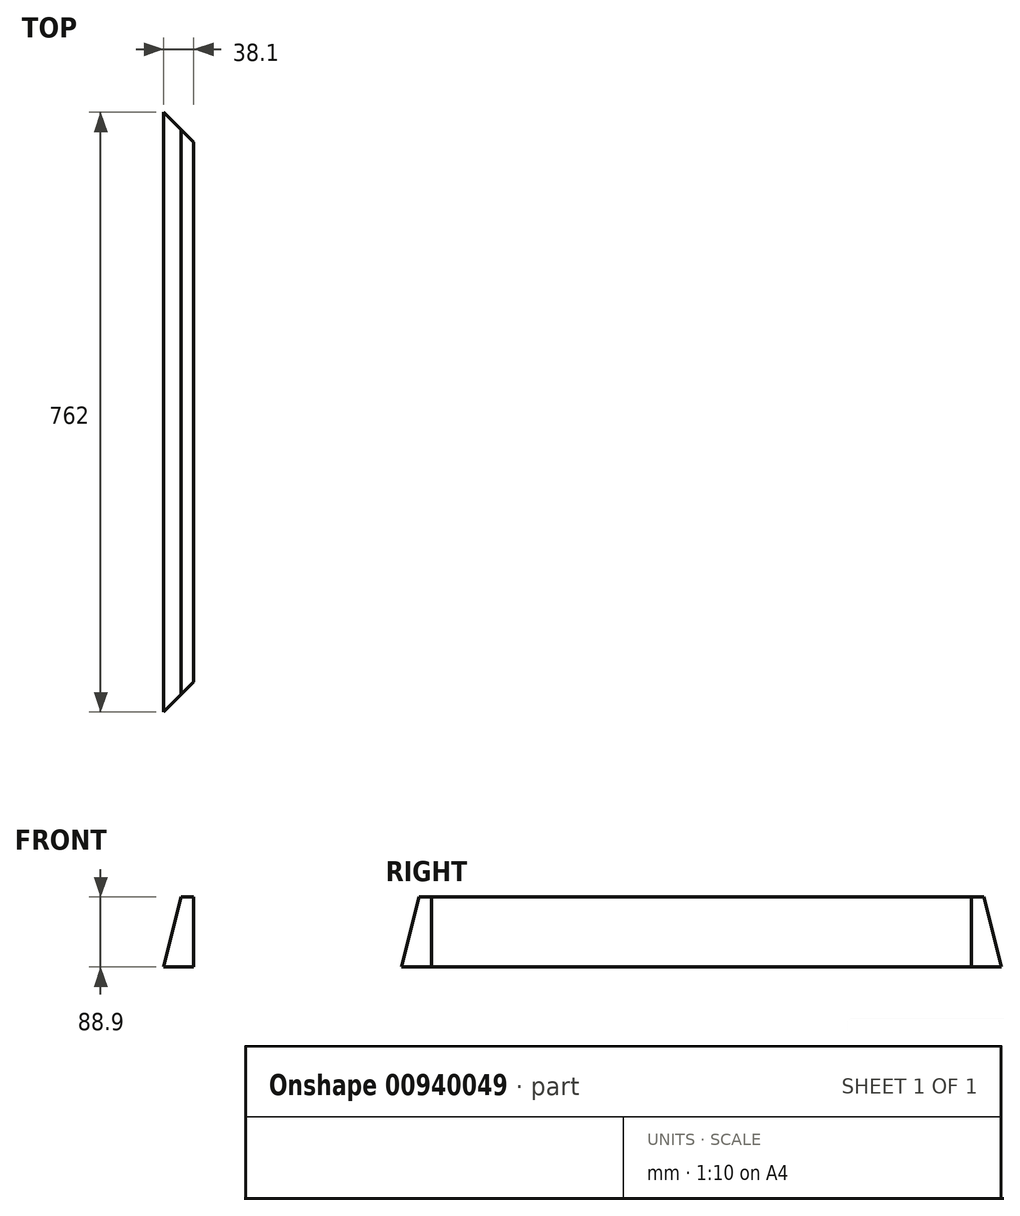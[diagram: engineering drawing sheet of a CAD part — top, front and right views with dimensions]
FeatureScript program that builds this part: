
annotation { "Feature Type Name" : "Feature", "Feature Type Description" : "" }
export const myFeature = defineFeature(function(context is Context, id is Id, definition is map)
    precondition{}
    {
        {
            var Q0;
            Q0=qCreatedBy(makeId("Front.planeOp"),FACE);
            var sketch = newSketch(context, id + "F0", { "sketchPlane" : qUnion([Q0])});
            skLineSegment(sketch, "E0.bottom", {"start": v(38.1, 44.45) * mm, "end": v(-38.1, 44.45) * mm});
            skLineSegment(sketch, "E0.top", {"start": v(38.1, -44.45) * mm, "end": v(-38.1, -44.45) * mm});
            skLineSegment(sketch, "E0.left", {"start": v(44.45, 38.1) * mm, "end": v(44.45, -38.1) * mm});
            skLineSegment(sketch, "E0.right", {"start": v(-44.45, 38.1) * mm, "end": v(-44.45, -38.1) * mm});
            skPoint(sketch, "E0.middle", {"position": v(0, 0) * mm});
            skPoint(sketch, "E1.visualSharp", {"position": v(-44.45, 44.45) * mm});
            skArc(sketch, "E1.filletArc", {"start": v(-38.1, 44.45) * mm, "mid": v(-42.6, 42.6) * mm, "end": v(-44.45, 38.1) * mm});
            skPoint(sketch, "E2.visualSharp", {"position": v(44.45, 44.45) * mm});
            skArc(sketch, "E2.filletArc", {"start": v(44.45, 38.1) * mm, "mid": v(42.6, 42.6) * mm, "end": v(38.1, 44.45) * mm});
            skPoint(sketch, "E3.visualSharp", {"position": v(44.45, -44.45) * mm});
            skArc(sketch, "E3.filletArc", {"start": v(38.1, -44.45) * mm, "mid": v(42.6, -42.6) * mm, "end": v(44.45, -38.1) * mm});
            skPoint(sketch, "E4.visualSharp", {"position": v(-44.45, -44.45) * mm});
            skArc(sketch, "E4.filletArc", {"start": v(-44.45, -38.1) * mm, "mid": v(-42.6, -42.6) * mm, "end": v(-38.1, -44.45) * mm});
            skLineSegment(sketch, "E5", {"start": v(0, -44.45) * mm, "end": v(0, 107.95) * mm});
            skLineSegment(sketch, "E6", {"start": v(0, 107.95) * mm, "end": v(38.1, -44.45) * mm});
            skLineSegment(sketch, "E7", {"start": v(0, 107.95) * mm, "end": v(-38.1, -44.45) * mm});
            skSolve(sketch);
        }
        {
            var Q0;
            {var subQ3=sQuery(id+"F0.wireOp",EDGE,"E0.bottom");var subQ7=sQuery(id+"F0.wireOp",EDGE,"E7");var subQ9=makeQuery(id+"F0.imprint","INTERSECT",VERTEX,{"derivedFrom":[subQ3,subQ7]});Q0=makeQuery(id+"F0.imprint","IMPRINT",FACE,{"disambiguationData":[TD([[makeQuery(id+"F0.imprint","IMPRINT",EDGE,{"disambiguationData":[TD([[subQ9,1.0]])],"derivedFrom":subQ3}),1.0]])]});}
            extrude(context, id + "F1", {"entities" : qUnion([Q0]), "depth" : 762 * mm, "offsetDistance" : 25.4 * mm});
        }
        {
            var Q0;
            Q0=makeQuery(id+"F1.opExtrude","SWEPT_FACE",FACE,{"disambiguationData":[OSD([sQuery(id+"F0.wireOp",EDGE,"E0.top")])]});
            var sketch = newSketch(context, id + "F2", { "sketchPlane" : qUnion([Q0])});
            skLineSegment(sketch, "E8", {"start": v(-38.1, 0) * mm, "end": v(0, 38.1) * mm});
            skLineSegment(sketch, "E9.0", {"start": v(0, 762) * mm, "end": v(0, 0) * mm});
            skLineSegment(sketch, "E10.0", {"start": v(0, 0) * mm, "end": v(-38.1, 0) * mm});
            skLineSegment(sketch, "E11", {"start": v(-38.1, 381) * mm, "end": v(0, 381) * mm});
            skLineSegment(sketch, "E12.MirrorCS", {"start": v(-38.1, 762) * mm, "end": v(0, 723.9) * mm});
            skSolve(sketch);
        }
        {
            var Q0;
            {var subQ2=sQuery(id+"F2.wireOp",EDGE,"E12.MirrorCS");Q0=makeQuery(id+"F2.imprint","IMPRINT",FACE,{"disambiguationData":[TD([[makeQuery(id+"F2.imprint","IMPRINT",EDGE,{"derivedFrom":subQ2}),1.0]])]});}
            var Q1;
            {var subQ0=sQuery(id+"F2.wireOp",EDGE,"E8");Q1=makeQuery(id+"F2.imprint","IMPRINT",FACE,{"disambiguationData":[TD([[makeQuery(id+"F2.imprint","IMPRINT",EDGE,{"derivedFrom":subQ0}),-1.0]])]});}
            extrude(context, id + "F3", {"entities" : qUnion([Q0, Q1]), "operationType" : NewBodyOperationType.REMOVE, "oppositeDirection" : true, "depth" : 101.6 * mm, "offsetDistance" : 25.4 * mm});
        }
    });
